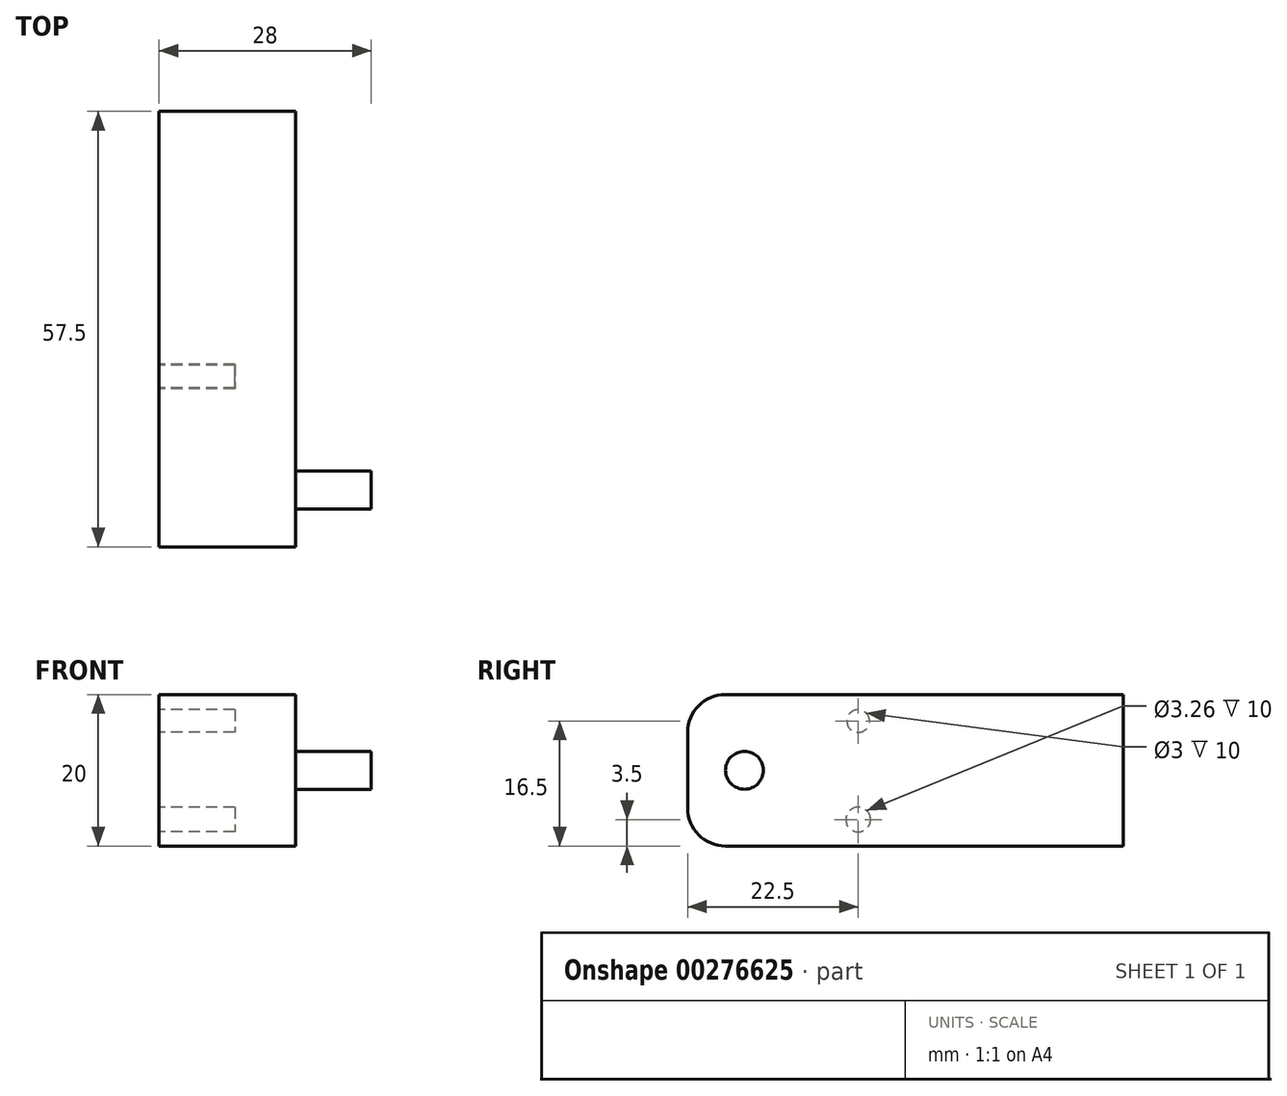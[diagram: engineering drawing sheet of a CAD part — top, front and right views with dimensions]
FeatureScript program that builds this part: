
annotation { "Feature Type Name" : "Feature", "Feature Type Description" : "" }
export const myFeature = defineFeature(function(context is Context, id is Id, definition is map)
    precondition{}
    {
        {
            var Q0;
            Q0=qCreatedBy(makeId("Right.planeOp"),FACE);
            var sketch = newSketch(context, id + "F0", { "sketchPlane" : qUnion([Q0])});
            skCircle(sketch, "E0", {"center": v(0, 0) * mm, "radius": 2.5 * mm});
            skLineSegment(sketch, "E1", {"start": v(-7.5, 10) * mm, "end": v(-7.5, -10) * mm});
            skLineSegment(sketch, "E2", {"start": v(-7.5, -10) * mm, "end": v(50, -10) * mm});
            skLineSegment(sketch, "E3", {"start": v(50, -10) * mm, "end": v(50, 10) * mm});
            skLineSegment(sketch, "E4", {"start": v(50, 10) * mm, "end": v(-7.5, 10) * mm});
            skLineSegment(sketch, "E5", {"start": v(0, 0) * mm, "end": v(-7.5, 0) * mm, "construction": true});
            skSolve(sketch);
        }
        {
            var Q0;
            Q0 = qSketchRegion(id + "F0", true);
            var Q1;
            Q1=makeQuery(id+"F0.imprint","IMPRINT",FACE,{"disambiguationData":[TD([[makeQuery(id+"F0.imprint","IMPRINT",EDGE,{"derivedFrom":sQuery(id+"F0.wireOp",EDGE,"E0")}),1.0]])]});
            extrude(context, id + "F1", {"entities" : qUnion([Q0, Q1]), "endBound" : BoundingType.SYMMETRIC, "depth" : 18 * mm});
        }
        {
            var Q0;
            Q0=makeQuery(id+"F1.opExtrude","SWEPT_EDGE",EDGE,{"disambiguationData":[OSD([sQuery(id+"F0.wireOp",EDGE,"E1"),sQuery(id+"F0.wireOp",EDGE,"E4")])]});
            var Q1;
            Q1=makeQuery(id+"F1.opExtrude","SWEPT_EDGE",EDGE,{"disambiguationData":[OSD([sQuery(id+"F0.wireOp",EDGE,"E1"),sQuery(id+"F0.wireOp",EDGE,"E2")])]});
            fillet(context, id + "F2", {"entities" : qUnion([Q0, Q1]), "radius" : 5 * mm, "tangentPropagation" : true, "allowEdgeOverflow" : false});
        }
        {
            var Q0;
            Q0=makeQuery(id+"F1.opExtrude","CAP_FACE",FACE,{"disambiguationData":[OSD([sQuery(id+"F0.wireOp",EDGE,"E1"),sQuery(id+"F0.wireOp",EDGE,"E2"),sQuery(id+"F0.wireOp",EDGE,"E3"),sQuery(id+"F0.wireOp",EDGE,"E4")])],"isStart":false});
            var sketch = newSketch(context, id + "F3", { "sketchPlane" : qUnion([Q0])});
            skCircle(sketch, "E6", {"center": v(0, 0) * mm, "radius": 2.5 * mm});
            skSolve(sketch);
        }
        {
            var Q0;
            Q0 = qSketchRegion(id + "F3", true);
            extrude(context, id + "F4", {"entities" : qUnion([Q0]), "operationType" : NewBodyOperationType.ADD, "depth" : 10 * mm});
        }
        {
            var Q0;
            Q0=makeQuery(id+"F1.opExtrude","CAP_FACE",FACE,{"disambiguationData":[OSD([sQuery(id+"F0.wireOp",EDGE,"E1"),sQuery(id+"F0.wireOp",EDGE,"E2"),sQuery(id+"F0.wireOp",EDGE,"E3"),sQuery(id+"F0.wireOp",EDGE,"E4")])],"isStart":true});
            var sketch = newSketch(context, id + "F5", { "sketchPlane" : qUnion([Q0])});
            skCircle(sketch, "E7", {"center": v(-15, 6.5) * mm, "radius": 1.5 * mm});
            skCircle(sketch, "E8", {"center": v(-15, -6.5) * mm, "radius": 1.63 * mm});
            skLineSegment(sketch, "E9", {"start": v(-15, -6.5) * mm, "end": v(-15, 6.5) * mm, "construction": true});
            skLineSegment(sketch, "E10", {"start": v(0, 0) * mm, "end": v(-15, 0) * mm, "construction": true});
            skSolve(sketch);
        }
        {
            var Q0;
            Q0 = qSketchRegion(id + "F5", true);
            extrude(context, id + "F6", {"entities" : qUnion([Q0]), "operationType" : NewBodyOperationType.REMOVE, "oppositeDirection" : true, "depth" : 10 * mm});
        }
    });
